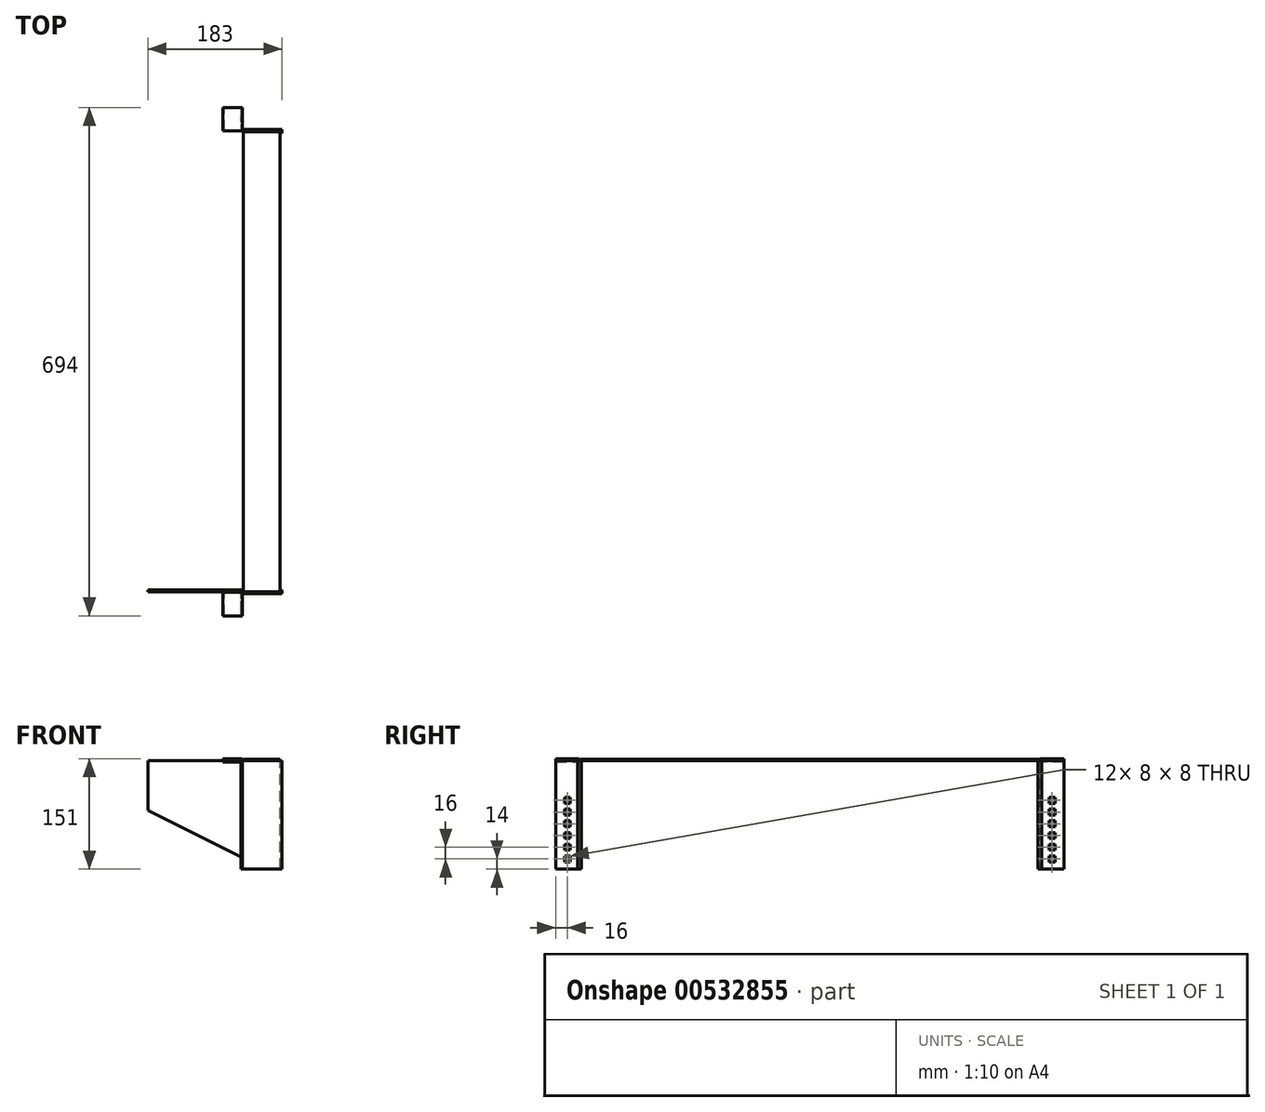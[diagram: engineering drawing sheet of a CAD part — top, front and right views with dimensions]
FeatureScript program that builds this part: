
annotation { "Feature Type Name" : "Feature", "Feature Type Description" : "" }
export const myFeature = defineFeature(function(context is Context, id is Id, definition is map)
    precondition{}
    {
        {
            var Q0;
            Q0=qCreatedBy(makeId("Right.planeOp"),FACE);
            var sketch = newSketch(context, id + "F0", { "sketchPlane" : qUnion([Q0])});
            skLineSegment(sketch, "E0.bottom", {"start": v(-314, 150) * mm, "end": v(314, 150) * mm});
            skLineSegment(sketch, "E0.top", {"start": v(-314, 148) * mm, "end": v(314, 148) * mm});
            skLineSegment(sketch, "E0.left", {"start": v(-314, 150) * mm, "end": v(-314, 148) * mm});
            skLineSegment(sketch, "E0.right", {"start": v(314, 150) * mm, "end": v(314, 148) * mm});
            skLineSegment(sketch, "E1.bottom", {"start": v(-314, 148) * mm, "end": v(-312, 148) * mm});
            skLineSegment(sketch, "E1.top", {"start": v(-314, 0) * mm, "end": v(-312, 0) * mm});
            skLineSegment(sketch, "E1.left", {"start": v(-314, 148) * mm, "end": v(-314, 0) * mm});
            skLineSegment(sketch, "E1.right", {"start": v(-312, 148) * mm, "end": v(-312, 0) * mm});
            skLineSegment(sketch, "E2.bottom", {"start": v(314, 148) * mm, "end": v(312, 148) * mm});
            skLineSegment(sketch, "E2.top", {"start": v(314, 0) * mm, "end": v(312, 0) * mm});
            skLineSegment(sketch, "E2.left", {"start": v(314, 148) * mm, "end": v(314, 0) * mm});
            skLineSegment(sketch, "E2.right", {"start": v(312, 148) * mm, "end": v(312, 0) * mm});
            skSolve(sketch);
        }
        {
            var Q0;
            Q0=makeQuery(id+"F0.imprint","IMPRINT",FACE,{"disambiguationData":[TD([[makeQuery(id+"F0.imprint","IMPRINT",EDGE,{"derivedFrom":sQuery(id+"F0.wireOp",EDGE,"E0.bottom")}),-1.0]])]});
            var Q1;
            Q1=makeQuery(id+"F0.imprint","IMPRINT",FACE,{"disambiguationData":[TD([[makeQuery(id+"F0.imprint","IMPRINT",EDGE,{"derivedFrom":sQuery(id+"F0.wireOp",EDGE,"E2.bottom")}),1.0]])]});
            var Q2;
            Q2=makeQuery(id+"F0.imprint","IMPRINT",FACE,{"disambiguationData":[TD([[makeQuery(id+"F0.imprint","IMPRINT",EDGE,{"derivedFrom":sQuery(id+"F0.wireOp",EDGE,"E1.bottom")}),-1.0]])]});
            extrude(context, id + "F1", {"entities" : qUnion([Q0, Q1, Q2]), "oppositeDirection" : true, "depth" : 50 * mm});
        }
        {
            var Q0;
            Q0=makeQuery(id+"F1.opExtrude","CAP_FACE",FACE,{"disambiguationData":[OSD([sQuery(id+"F0.wireOp",EDGE,"E0.bottom"),sQuery(id+"F0.wireOp",EDGE,"E0.top"),sQuery(id+"F0.wireOp",EDGE,"E0.left"),sQuery(id+"F0.wireOp",EDGE,"E0.right"),sQuery(id+"F0.wireOp",EDGE,"E1.top"),sQuery(id+"F0.wireOp",EDGE,"E1.left"),sQuery(id+"F0.wireOp",EDGE,"E1.right"),sQuery(id+"F0.wireOp",EDGE,"E2.top"),sQuery(id+"F0.wireOp",EDGE,"E2.left"),sQuery(id+"F0.wireOp",EDGE,"E2.right")])],"isStart":false});
            var sketch = newSketch(context, id + "F2", { "sketchPlane" : qUnion([Q0])});
            skLineSegment(sketch, "E3.bottom", {"start": v(314, 0) * mm, "end": v(312, 0) * mm});
            skLineSegment(sketch, "E3.top", {"start": v(314, 150) * mm, "end": v(312, 150) * mm});
            skLineSegment(sketch, "E3.left", {"start": v(314, 0) * mm, "end": v(314, 150) * mm});
            skLineSegment(sketch, "E3.right", {"start": v(312, 0) * mm, "end": v(312, 150) * mm});
            skLineSegment(sketch, "E4.bottom", {"start": v(-312, 0) * mm, "end": v(-314, 0) * mm});
            skLineSegment(sketch, "E4.top", {"start": v(-312, 150) * mm, "end": v(-314, 150) * mm});
            skLineSegment(sketch, "E4.left", {"start": v(-312, 0) * mm, "end": v(-312, 150) * mm});
            skLineSegment(sketch, "E4.right", {"start": v(-314, 0) * mm, "end": v(-314, 150) * mm});
            skSolve(sketch);
        }
        {
            var Q0;
            {var subQ2=sQuery(id+"F2.wireOp",EDGE,"E3.bottom");Q0=makeQuery(id+"F2.imprint","IMPRINT",FACE,{"disambiguationData":[TD([[makeQuery(id+"F2.imprint","IMPRINT",EDGE,{"derivedFrom":subQ2}),-1.0]])]});}
            var Q1;
            {var subQ3=sQuery(id+"F2.wireOp",EDGE,"E4.bottom");Q1=makeQuery(id+"F2.imprint","IMPRINT",FACE,{"disambiguationData":[TD([[makeQuery(id+"F2.imprint","IMPRINT",EDGE,{"derivedFrom":subQ3}),1.0]])]});}
            extrude(context, id + "F3", {"entities" : qUnion([Q0, Q1]), "operationType" : NewBodyOperationType.ADD, "depth" : 130 * mm});
        }
        {
            var Q0;
            Q0=makeQuery(id+"F1.opExtrude","CAP_FACE",FACE,{"disambiguationData":[OSD([sQuery(id+"F0.wireOp",EDGE,"E0.bottom"),sQuery(id+"F0.wireOp",EDGE,"E0.top"),sQuery(id+"F0.wireOp",EDGE,"E0.left"),sQuery(id+"F0.wireOp",EDGE,"E0.right"),sQuery(id+"F0.wireOp",EDGE,"E1.top"),sQuery(id+"F0.wireOp",EDGE,"E1.left"),sQuery(id+"F0.wireOp",EDGE,"E1.right"),sQuery(id+"F0.wireOp",EDGE,"E2.top"),sQuery(id+"F0.wireOp",EDGE,"E2.left"),sQuery(id+"F0.wireOp",EDGE,"E2.right")])],"isStart":true});
            var sketch = newSketch(context, id + "F4", { "sketchPlane" : qUnion([Q0])});
            skLineSegment(sketch, "E5.bottom", {"start": v(314, 0) * mm, "end": v(312, 0) * mm});
            skLineSegment(sketch, "E5.top", {"start": v(314, 148) * mm, "end": v(312, 148) * mm});
            skLineSegment(sketch, "E5.left", {"start": v(314, 0) * mm, "end": v(314, 148) * mm});
            skLineSegment(sketch, "E5.right", {"start": v(312, 0) * mm, "end": v(312, 148) * mm});
            skLineSegment(sketch, "E6.bottom", {"start": v(-312, 0) * mm, "end": v(-314, 0) * mm});
            skLineSegment(sketch, "E6.top", {"start": v(-312, 148) * mm, "end": v(-314, 148) * mm});
            skLineSegment(sketch, "E6.left", {"start": v(-312, 0) * mm, "end": v(-312, 148) * mm});
            skLineSegment(sketch, "E6.right", {"start": v(-314, 0) * mm, "end": v(-314, 148) * mm});
            skSolve(sketch);
        }
        {
            var Q0;
            Q0=makeQuery(id+"F4.imprint","IMPRINT",FACE,{"disambiguationData":[TD([[makeQuery(id+"F4.imprint","IMPRINT",EDGE,{"derivedFrom":sQuery(id+"F4.wireOp",EDGE,"E5.bottom")}),-1.0]])]});
            var Q1;
            Q1=makeQuery(id+"F4.imprint","IMPRINT",FACE,{"disambiguationData":[TD([[makeQuery(id+"F4.imprint","IMPRINT",EDGE,{"derivedFrom":sQuery(id+"F4.wireOp",EDGE,"E6.bottom")}),1.0]])]});
            extrude(context, id + "F5", {"entities" : qUnion([Q0, Q1]), "operationType" : NewBodyOperationType.ADD, "depth" : 3 * mm});
        }
        {
            var Q0;
            Q0=makeQuery(id+"F5.boolean.opBoolean","MERGE",FACE,{"derivedFrom":[makeQuery(id+"F3.boolean.opBoolean","MERGE",FACE,{"derivedFrom":[makeQuery(id+"F1.opExtrude","SWEPT_FACE",FACE,{"disambiguationData":[OSD([sQuery(id+"F0.wireOp",EDGE,"E1.right")])]}),makeQuery(id+"F3.opExtrude","SWEPT_FACE",FACE,{"disambiguationData":[OSD([sQuery(id+"F2.wireOp",EDGE,"E3.right")])]})]}),makeQuery(id+"F5.opExtrude","SWEPT_FACE",FACE,{"disambiguationData":[OSD([sQuery(id+"F4.wireOp",EDGE,"E6.left")])]})]});
            var sketch = newSketch(context, id + "F6", { "sketchPlane" : qUnion([Q0])});
            skLineSegment(sketch, "E7.bottom", {"start": v(-3, 148) * mm, "end": v(-1, 148) * mm});
            skLineSegment(sketch, "E7.top", {"start": v(-3, 0) * mm, "end": v(-1, 0) * mm});
            skLineSegment(sketch, "E7.left", {"start": v(-3, 148) * mm, "end": v(-3, 0) * mm});
            skLineSegment(sketch, "E7.right", {"start": v(-1, 148) * mm, "end": v(-1, 0) * mm});
            skSolve(sketch);
        }
        {
            var Q0;
            Q0=makeQuery(id+"F6.imprint","IMPRINT",FACE,{"disambiguationData":[TD([[makeQuery(id+"F6.imprint","IMPRINT",EDGE,{"derivedFrom":sQuery(id+"F6.wireOp",EDGE,"E7.bottom")}),-1.0]])]});
            extrude(context, id + "F7", {"entities" : qUnion([Q0]), "operationType" : NewBodyOperationType.ADD, "oppositeDirection" : true, "depth" : 5 * mm});
        }
        {
            var Q0;
            Q0=makeQuery(id+"F7.opExtrude","SWEPT_FACE",FACE,{"disambiguationData":[OSD([sQuery(id+"F6.wireOp",EDGE,"E7.right")])]});
            var sketch = newSketch(context, id + "F8", { "sketchPlane" : qUnion([Q0])});
            skLineSegment(sketch, "E8.bottom", {"start": v(315, 0) * mm, "end": v(317, 0) * mm});
            skLineSegment(sketch, "E8.top", {"start": v(315, 148) * mm, "end": v(317, 148) * mm});
            skLineSegment(sketch, "E8.left", {"start": v(317, 0) * mm, "end": v(317, 148) * mm});
            skLineSegment(sketch, "E8.right", {"start": v(315, 0) * mm, "end": v(315, 148) * mm});
            skSolve(sketch);
        }
        {
            var Q0;
            Q0=makeQuery(id+"F8.imprint","IMPRINT",FACE,{"disambiguationData":[TD([[makeQuery(id+"F8.imprint","IMPRINT",EDGE,{"derivedFrom":sQuery(id+"F8.wireOp",EDGE,"E8.bottom")}),-1.0]])]});
            extrude(context, id + "F9", {"entities" : qUnion([Q0]), "operationType" : NewBodyOperationType.ADD, "depth" : 54 * mm});
        }
        {
            var Q0;
            Q0=makeQuery(id+"F9.boolean.opBoolean","MERGE",FACE,{"derivedFrom":[makeQuery(id+"F7.opExtrude","CAP_FACE",FACE,{"disambiguationData":[OSD([sQuery(id+"F6.wireOp",EDGE,"E7.bottom"),sQuery(id+"F6.wireOp",EDGE,"E7.top"),sQuery(id+"F6.wireOp",EDGE,"E7.left"),sQuery(id+"F6.wireOp",EDGE,"E7.right")])],"isStart":false}),makeQuery(id+"F9.opExtrude","SWEPT_FACE",FACE,{"disambiguationData":[OSD([sQuery(id+"F8.wireOp",EDGE,"E8.left")])]})]});
            var sketch = newSketch(context, id + "F10", { "sketchPlane" : qUnion([Q0])});
            skLineSegment(sketch, "E9.bottom", {"start": v(-53, 148) * mm, "end": v(-51, 148) * mm});
            skLineSegment(sketch, "E9.top", {"start": v(-53, 0) * mm, "end": v(-51, 0) * mm});
            skLineSegment(sketch, "E9.left", {"start": v(-53, 148) * mm, "end": v(-53, 0) * mm});
            skLineSegment(sketch, "E9.right", {"start": v(-51, 148) * mm, "end": v(-51, 0) * mm});
            skSolve(sketch);
        }
        {
            var Q0;
            Q0=makeQuery(id+"F10.imprint","IMPRINT",FACE,{"disambiguationData":[TD([[makeQuery(id+"F10.imprint","IMPRINT",EDGE,{"derivedFrom":sQuery(id+"F10.wireOp",EDGE,"E9.bottom")}),1.0]])]});
            extrude(context, id + "F11", {"entities" : qUnion([Q0]), "operationType" : NewBodyOperationType.ADD, "depth" : 30 * mm});
        }
        {
            var Q0;
            Q0=makeQuery(id+"F5.boolean.opBoolean","MERGE",FACE,{"derivedFrom":[makeQuery(id+"F3.boolean.opBoolean","MERGE",FACE,{"derivedFrom":[makeQuery(id+"F1.opExtrude","SWEPT_FACE",FACE,{"disambiguationData":[OSD([sQuery(id+"F0.wireOp",EDGE,"E0.left"),sQuery(id+"F0.wireOp",EDGE,"E1.left")])]}),makeQuery(id+"F3.opExtrude","SWEPT_FACE",FACE,{"disambiguationData":[OSD([sQuery(id+"F2.wireOp",EDGE,"E3.left")])]})]}),makeQuery(id+"F5.opExtrude","SWEPT_FACE",FACE,{"disambiguationData":[OSD([sQuery(id+"F4.wireOp",EDGE,"E6.right")])]})]});
            var sketch = newSketch(context, id + "F12", { "sketchPlane" : qUnion([Q0])});
            skLineSegment(sketch, "E10", {"start": v(0, 0) * mm, "end": v(-20, 0) * mm});
            skLineSegment(sketch, "E11", {"start": v(-20, 0) * mm, "end": v(-180, 80) * mm});
            skLineSegment(sketch, "E12", {"start": v(-180, 80) * mm, "end": v(-180, 0) * mm});
            skLineSegment(sketch, "E13", {"start": v(-180, 0) * mm, "end": v(-20, 0) * mm});
            skSolve(sketch);
        }
        {
            var Q0;
            Q0=makeQuery(id+"F12.imprint","IMPRINT",FACE,{"disambiguationData":[TD([[makeQuery(id+"F12.imprint","IMPRINT",EDGE,{"derivedFrom":sQuery(id+"F12.wireOp",EDGE,"E11")}),1.0]])]});
            extrude(context, id + "F13", {"entities" : qUnion([Q0]), "operationType" : NewBodyOperationType.REMOVE, "oppositeDirection" : true, "depth" : 761 * mm});
        }
        {
            var Q0;
            Q0=makeQuery(id+"F5.boolean.opBoolean","MERGE",FACE,{"derivedFrom":[makeQuery(id+"F3.boolean.opBoolean","MERGE",FACE,{"derivedFrom":[makeQuery(id+"F1.opExtrude","SWEPT_FACE",FACE,{"disambiguationData":[OSD([sQuery(id+"F0.wireOp",EDGE,"E0.right"),sQuery(id+"F0.wireOp",EDGE,"E2.left")])]}),makeQuery(id+"F3.opExtrude","SWEPT_FACE",FACE,{"disambiguationData":[OSD([sQuery(id+"F2.wireOp",EDGE,"E4.right")])]})]}),makeQuery(id+"F5.opExtrude","SWEPT_FACE",FACE,{"disambiguationData":[OSD([sQuery(id+"F4.wireOp",EDGE,"E5.left")])]})]});
            var sketch = newSketch(context, id + "F14", { "sketchPlane" : qUnion([Q0])});
            skLineSegment(sketch, "E14.bottom", {"start": v(-3, 148) * mm, "end": v(-1, 148) * mm});
            skLineSegment(sketch, "E14.top", {"start": v(-3, 0) * mm, "end": v(-1, 0) * mm});
            skLineSegment(sketch, "E14.left", {"start": v(-3, 148) * mm, "end": v(-3, 0) * mm});
            skLineSegment(sketch, "E14.right", {"start": v(-1, 148) * mm, "end": v(-1, 0) * mm});
            skSolve(sketch);
        }
        {
            var Q0;
            Q0=makeQuery(id+"F14.imprint","IMPRINT",FACE,{"disambiguationData":[TD([[makeQuery(id+"F14.imprint","IMPRINT",EDGE,{"derivedFrom":sQuery(id+"F14.wireOp",EDGE,"E14.bottom")}),-1.0]])]});
            extrude(context, id + "F15", {"entities" : qUnion([Q0]), "operationType" : NewBodyOperationType.ADD, "depth" : 3 * mm});
        }
        {
            var Q0;
            Q0=makeQuery(id+"F15.opExtrude","SWEPT_FACE",FACE,{"disambiguationData":[OSD([sQuery(id+"F14.wireOp",EDGE,"E14.right")])]});
            var sketch = newSketch(context, id + "F16", { "sketchPlane" : qUnion([Q0])});
            skLineSegment(sketch, "E15.bottom", {"start": v(-317, 148) * mm, "end": v(-315, 148) * mm});
            skLineSegment(sketch, "E15.top", {"start": v(-317, 0) * mm, "end": v(-315, 0) * mm});
            skLineSegment(sketch, "E15.left", {"start": v(-317, 148) * mm, "end": v(-317, 0) * mm});
            skLineSegment(sketch, "E15.right", {"start": v(-315, 148) * mm, "end": v(-315, 0) * mm});
            skSolve(sketch);
        }
        {
            var Q0;
            Q0=qSketchRegion(id+"F16",true);
            extrude(context, id + "F17", {"entities" : qUnion([Q0]), "operationType" : NewBodyOperationType.ADD, "depth" : 54 * mm});
        }
        {
            var Q0;
            Q0=makeQuery(id+"F17.boolean.opBoolean","MERGE",FACE,{"derivedFrom":[makeQuery(id+"F15.opExtrude","CAP_FACE",FACE,{"disambiguationData":[OSD([sQuery(id+"F14.wireOp",EDGE,"E14.bottom"),sQuery(id+"F14.wireOp",EDGE,"E14.top"),sQuery(id+"F14.wireOp",EDGE,"E14.left"),sQuery(id+"F14.wireOp",EDGE,"E14.right")])],"isStart":false}),makeQuery(id+"F17.opExtrude","SWEPT_FACE",FACE,{"disambiguationData":[OSD([sQuery(id+"F16.wireOp",EDGE,"E15.left")])]})]});
            var sketch = newSketch(context, id + "F18", { "sketchPlane" : qUnion([Q0])});
            skLineSegment(sketch, "E16.bottom", {"start": v(53, 148) * mm, "end": v(51, 148) * mm});
            skLineSegment(sketch, "E16.top", {"start": v(53, 0) * mm, "end": v(51, 0) * mm});
            skLineSegment(sketch, "E16.left", {"start": v(53, 148) * mm, "end": v(53, 0) * mm});
            skLineSegment(sketch, "E16.right", {"start": v(51, 148) * mm, "end": v(51, 0) * mm});
            skSolve(sketch);
        }
        {
            var Q0;
            Q0=makeQuery(id+"F18.imprint","IMPRINT",FACE,{"disambiguationData":[TD([[makeQuery(id+"F18.imprint","IMPRINT",EDGE,{"derivedFrom":sQuery(id+"F18.wireOp",EDGE,"E16.bottom")}),-1.0]])]});
            extrude(context, id + "F19", {"entities" : qUnion([Q0]), "operationType" : NewBodyOperationType.ADD, "depth" : 30 * mm});
        }
        {
            var Q0;
            Q0=makeQuery(id+"F19.boolean.opBoolean","MERGE",FACE,{"derivedFrom":[makeQuery(id+"F17.opExtrude","CAP_FACE",FACE,{"disambiguationData":[OSD([sQuery(id+"F16.wireOp",EDGE,"E15.bottom"),sQuery(id+"F16.wireOp",EDGE,"E15.top"),sQuery(id+"F16.wireOp",EDGE,"E15.left"),sQuery(id+"F16.wireOp",EDGE,"E15.right")])],"isStart":false}),makeQuery(id+"F19.opExtrude","SWEPT_FACE",FACE,{"disambiguationData":[OSD([sQuery(id+"F18.wireOp",EDGE,"E16.left")])]})]});
            var sketch = newSketch(context, id + "F20", { "sketchPlane" : qUnion([Q0])});
            skLineSegment(sketch, "E17.bottom", {"start": v(-347, 148) * mm, "end": v(-315, 148) * mm});
            skLineSegment(sketch, "E17.top", {"start": v(-347, 146) * mm, "end": v(-315, 146) * mm});
            skLineSegment(sketch, "E17.left", {"start": v(-347, 148) * mm, "end": v(-347, 146) * mm});
            skLineSegment(sketch, "E17.right", {"start": v(-315, 148) * mm, "end": v(-315, 146) * mm});
            skSolve(sketch);
        }
        {
            var Q0;
            Q0=makeQuery(id+"F20.imprint","IMPRINT",FACE,{"disambiguationData":[TD([[makeQuery(id+"F20.imprint","IMPRINT",EDGE,{"derivedFrom":sQuery(id+"F20.wireOp",EDGE,"E17.bottom")}),-1.0]])]});
            extrude(context, id + "F21", {"entities" : qUnion([Q0]), "operationType" : NewBodyOperationType.ADD, "depth" : 25 * mm});
        }
        {
            var Q0;
            Q0=makeQuery(id+"F21.boolean.opBoolean","MERGE",FACE,{"derivedFrom":[makeQuery(id+"F19.boolean.opBoolean","MERGE",FACE,{"derivedFrom":[makeQuery(id+"F17.boolean.opBoolean","MERGE",FACE,{"derivedFrom":[makeQuery(id+"F15.boolean.opBoolean","MERGE",FACE,{"derivedFrom":[makeQuery(id+"F5.opExtrude","SWEPT_FACE",FACE,{"disambiguationData":[OSD([sQuery(id+"F4.wireOp",EDGE,"E5.top")])]}),makeQuery(id+"F15.opExtrude","SWEPT_FACE",FACE,{"disambiguationData":[OSD([sQuery(id+"F14.wireOp",EDGE,"E14.bottom")])]})]}),makeQuery(id+"F17.opExtrude","SWEPT_FACE",FACE,{"disambiguationData":[OSD([sQuery(id+"F16.wireOp",EDGE,"E15.bottom")])]})]}),makeQuery(id+"F19.opExtrude","SWEPT_FACE",FACE,{"disambiguationData":[OSD([sQuery(id+"F18.wireOp",EDGE,"E16.bottom")])]})]}),makeQuery(id+"F21.opExtrude","SWEPT_FACE",FACE,{"disambiguationData":[OSD([sQuery(id+"F20.wireOp",EDGE,"E17.bottom")])]})]});
            var sketch = newSketch(context, id + "F22", { "sketchPlane" : qUnion([Q0])});
            skLineSegment(sketch, "E18.bottom", {"start": v(-78, 315) * mm, "end": v(-76, 315) * mm});
            skLineSegment(sketch, "E18.top", {"start": v(-78, 347) * mm, "end": v(-76, 347) * mm});
            skLineSegment(sketch, "E18.left", {"start": v(-78, 315) * mm, "end": v(-78, 347) * mm});
            skLineSegment(sketch, "E18.right", {"start": v(-76, 315) * mm, "end": v(-76, 347) * mm});
            skSolve(sketch);
        }
        {
            var Q0;
            Q0=makeQuery(id+"F22.imprint","IMPRINT",FACE,{"disambiguationData":[TD([[makeQuery(id+"F22.imprint","IMPRINT",EDGE,{"derivedFrom":sQuery(id+"F22.wireOp",EDGE,"E18.bottom")}),1.0]])]});
            extrude(context, id + "F23", {"entities" : qUnion([Q0]), "operationType" : NewBodyOperationType.ADD, "depth" : 3 * mm});
        }
        {
            var Q0;
            Q0=makeQuery(id+"F23.opExtrude","SWEPT_FACE",FACE,{"disambiguationData":[OSD([sQuery(id+"F22.wireOp",EDGE,"E18.right")])]});
            var sketch = newSketch(context, id + "F24", { "sketchPlane" : qUnion([Q0])});
            skLineSegment(sketch, "E19.bottom", {"start": v(347, 151) * mm, "end": v(315, 151) * mm});
            skLineSegment(sketch, "E19.top", {"start": v(347, 149) * mm, "end": v(315, 149) * mm});
            skLineSegment(sketch, "E19.left", {"start": v(347, 151) * mm, "end": v(347, 149) * mm});
            skLineSegment(sketch, "E19.right", {"start": v(315, 151) * mm, "end": v(315, 149) * mm});
            skSolve(sketch);
        }
        {
            var Q0;
            Q0=makeQuery(id+"F24.imprint","IMPRINT",FACE,{"disambiguationData":[TD([[makeQuery(id+"F24.imprint","IMPRINT",EDGE,{"derivedFrom":sQuery(id+"F24.wireOp",EDGE,"E19.bottom")}),-1.0]])]});
            extrude(context, id + "F25", {"entities" : qUnion([Q0]), "operationType" : NewBodyOperationType.ADD, "depth" : 25 * mm});
        }
        {
            var Q0;
            Q0=makeQuery(id+"F19.boolean.opBoolean","MERGE",FACE,{"derivedFrom":[makeQuery(id+"F17.opExtrude","CAP_FACE",FACE,{"disambiguationData":[OSD([sQuery(id+"F16.wireOp",EDGE,"E15.bottom"),sQuery(id+"F16.wireOp",EDGE,"E15.top"),sQuery(id+"F16.wireOp",EDGE,"E15.left"),sQuery(id+"F16.wireOp",EDGE,"E15.right")])],"isStart":false}),makeQuery(id+"F19.opExtrude","SWEPT_FACE",FACE,{"disambiguationData":[OSD([sQuery(id+"F18.wireOp",EDGE,"E16.left")])]})]});
            var sketch = newSketch(context, id + "F26", { "sketchPlane" : qUnion([Q0])});
            skLineSegment(sketch, "E20.bottom", {"start": v(-327, 10) * mm, "end": v(-335, 10) * mm});
            skLineSegment(sketch, "E20.top", {"start": v(-327, 18) * mm, "end": v(-335, 18) * mm});
            skLineSegment(sketch, "E20.left", {"start": v(-327, 10) * mm, "end": v(-327, 18) * mm});
            skLineSegment(sketch, "E20.right", {"start": v(-335, 10) * mm, "end": v(-335, 18) * mm});
            skLineSegment(sketch, "E21.bottom", {"start": v(-327, 26) * mm, "end": v(-335, 26) * mm});
            skLineSegment(sketch, "E21.top", {"start": v(-327, 34) * mm, "end": v(-335, 34) * mm});
            skLineSegment(sketch, "E21.left", {"start": v(-327, 26) * mm, "end": v(-327, 34) * mm});
            skLineSegment(sketch, "E21.right", {"start": v(-335, 26) * mm, "end": v(-335, 34) * mm});
            skLineSegment(sketch, "E22.bottom", {"start": v(-327, 42) * mm, "end": v(-335, 42) * mm});
            skLineSegment(sketch, "E22.top", {"start": v(-327, 50) * mm, "end": v(-335, 50) * mm});
            skLineSegment(sketch, "E22.left", {"start": v(-327, 42) * mm, "end": v(-327, 50) * mm});
            skLineSegment(sketch, "E22.right", {"start": v(-335, 42) * mm, "end": v(-335, 50) * mm});
            skLineSegment(sketch, "E23.bottom", {"start": v(-327, 58) * mm, "end": v(-335, 58) * mm});
            skLineSegment(sketch, "E23.top", {"start": v(-327, 66) * mm, "end": v(-335, 66) * mm});
            skLineSegment(sketch, "E23.left", {"start": v(-327, 58) * mm, "end": v(-327, 66) * mm});
            skLineSegment(sketch, "E23.right", {"start": v(-335, 58) * mm, "end": v(-335, 66) * mm});
            skLineSegment(sketch, "E24.bottom", {"start": v(-335, 74) * mm, "end": v(-327, 74) * mm});
            skLineSegment(sketch, "E24.top", {"start": v(-335, 82) * mm, "end": v(-327, 82) * mm});
            skLineSegment(sketch, "E24.left", {"start": v(-335, 74) * mm, "end": v(-335, 82) * mm});
            skLineSegment(sketch, "E24.right", {"start": v(-327, 74) * mm, "end": v(-327, 82) * mm});
            skLineSegment(sketch, "E25.bottom", {"start": v(-327, 90) * mm, "end": v(-335, 90) * mm});
            skLineSegment(sketch, "E25.top", {"start": v(-327, 98) * mm, "end": v(-335, 98) * mm});
            skLineSegment(sketch, "E25.left", {"start": v(-327, 90) * mm, "end": v(-327, 98) * mm});
            skLineSegment(sketch, "E25.right", {"start": v(-335, 90) * mm, "end": v(-335, 98) * mm});
            skSolve(sketch);
        }
        {
            var Q0;
            Q0=makeQuery(id+"F26.imprint","IMPRINT",FACE,{"disambiguationData":[TD([[makeQuery(id+"F26.imprint","IMPRINT",EDGE,{"derivedFrom":sQuery(id+"F26.wireOp",EDGE,"E25.bottom")}),-1.0]])]});
            var Q1;
            Q1=makeQuery(id+"F26.imprint","IMPRINT",FACE,{"disambiguationData":[TD([[makeQuery(id+"F26.imprint","IMPRINT",EDGE,{"derivedFrom":sQuery(id+"F26.wireOp",EDGE,"E24.bottom")}),1.0]])]});
            var Q2;
            Q2=makeQuery(id+"F26.imprint","IMPRINT",FACE,{"disambiguationData":[TD([[makeQuery(id+"F26.imprint","IMPRINT",EDGE,{"derivedFrom":sQuery(id+"F26.wireOp",EDGE,"E23.bottom")}),-1.0]])]});
            var Q3;
            Q3=makeQuery(id+"F26.imprint","IMPRINT",FACE,{"disambiguationData":[TD([[makeQuery(id+"F26.imprint","IMPRINT",EDGE,{"derivedFrom":sQuery(id+"F26.wireOp",EDGE,"E22.bottom")}),-1.0]])]});
            var Q4;
            Q4=makeQuery(id+"F26.imprint","IMPRINT",FACE,{"disambiguationData":[TD([[makeQuery(id+"F26.imprint","IMPRINT",EDGE,{"derivedFrom":sQuery(id+"F26.wireOp",EDGE,"E21.bottom")}),-1.0]])]});
            var Q5;
            Q5=makeQuery(id+"F26.imprint","IMPRINT",FACE,{"disambiguationData":[TD([[makeQuery(id+"F26.imprint","IMPRINT",EDGE,{"derivedFrom":sQuery(id+"F26.wireOp",EDGE,"E20.bottom")}),-1.0]])]});
            extrude(context, id + "F27", {"entities" : qUnion([Q0, Q1, Q2, Q3, Q4, Q5]), "operationType" : NewBodyOperationType.REMOVE, "oppositeDirection" : true, "depth" : 25 * mm});
        }
        {
            var Q0;
            Q0=makeQuery(id+"F11.boolean.opBoolean","MERGE",FACE,{"derivedFrom":[makeQuery(id+"F9.opExtrude","CAP_FACE",FACE,{"disambiguationData":[OSD([sQuery(id+"F8.wireOp",EDGE,"E8.bottom"),sQuery(id+"F8.wireOp",EDGE,"E8.top"),sQuery(id+"F8.wireOp",EDGE,"E8.left"),sQuery(id+"F8.wireOp",EDGE,"E8.right")])],"isStart":false}),makeQuery(id+"F11.opExtrude","SWEPT_FACE",FACE,{"disambiguationData":[OSD([sQuery(id+"F10.wireOp",EDGE,"E9.left")])]})]});
            var sketch = newSketch(context, id + "F28", { "sketchPlane" : qUnion([Q0])});
            skLineSegment(sketch, "E26.bottom", {"start": v(347, 148) * mm, "end": v(315, 148) * mm});
            skLineSegment(sketch, "E26.top", {"start": v(347, 146) * mm, "end": v(315, 146) * mm});
            skLineSegment(sketch, "E26.left", {"start": v(347, 148) * mm, "end": v(347, 146) * mm});
            skLineSegment(sketch, "E26.right", {"start": v(315, 148) * mm, "end": v(315, 146) * mm});
            skSolve(sketch);
        }
        {
            var Q0;
            Q0=qSketchRegion(id+"F28",true);
            extrude(context, id + "F29", {"entities" : qUnion([Q0]), "operationType" : NewBodyOperationType.ADD, "depth" : 25 * mm});
        }
        {
            var Q0;
            Q0=makeQuery(id+"F29.boolean.opBoolean","MERGE",FACE,{"derivedFrom":[makeQuery(id+"F11.boolean.opBoolean","MERGE",FACE,{"derivedFrom":[makeQuery(id+"F9.boolean.opBoolean","MERGE",FACE,{"derivedFrom":[makeQuery(id+"F7.boolean.opBoolean","MERGE",FACE,{"derivedFrom":[makeQuery(id+"F5.opExtrude","SWEPT_FACE",FACE,{"disambiguationData":[OSD([sQuery(id+"F4.wireOp",EDGE,"E6.top")])]}),makeQuery(id+"F7.opExtrude","SWEPT_FACE",FACE,{"disambiguationData":[OSD([sQuery(id+"F6.wireOp",EDGE,"E7.bottom")])]})]}),makeQuery(id+"F9.opExtrude","SWEPT_FACE",FACE,{"disambiguationData":[OSD([sQuery(id+"F8.wireOp",EDGE,"E8.top")])]})]}),makeQuery(id+"F11.opExtrude","SWEPT_FACE",FACE,{"disambiguationData":[OSD([sQuery(id+"F10.wireOp",EDGE,"E9.bottom")])]})]}),makeQuery(id+"F29.opExtrude","SWEPT_FACE",FACE,{"disambiguationData":[OSD([sQuery(id+"F28.wireOp",EDGE,"E26.bottom")])]})]});
            var sketch = newSketch(context, id + "F30", { "sketchPlane" : qUnion([Q0])});
            skLineSegment(sketch, "E27.bottom", {"start": v(-78, -347) * mm, "end": v(-76, -347) * mm});
            skLineSegment(sketch, "E27.top", {"start": v(-78, -315) * mm, "end": v(-76, -315) * mm});
            skLineSegment(sketch, "E27.left", {"start": v(-78, -347) * mm, "end": v(-78, -315) * mm});
            skLineSegment(sketch, "E27.right", {"start": v(-76, -347) * mm, "end": v(-76, -315) * mm});
            skSolve(sketch);
        }
        {
            var Q0;
            Q0=qSketchRegion(id+"F30",true);
            extrude(context, id + "F31", {"entities" : qUnion([Q0]), "operationType" : NewBodyOperationType.ADD, "depth" : 3 * mm});
        }
        {
            var Q0;
            Q0=makeQuery(id+"F31.opExtrude","SWEPT_FACE",FACE,{"disambiguationData":[OSD([sQuery(id+"F30.wireOp",EDGE,"E27.right")])]});
            var sketch = newSketch(context, id + "F32", { "sketchPlane" : qUnion([Q0])});
            skLineSegment(sketch, "E28.bottom", {"start": v(-347, 151) * mm, "end": v(-315, 151) * mm});
            skLineSegment(sketch, "E28.top", {"start": v(-347, 149) * mm, "end": v(-315, 149) * mm});
            skLineSegment(sketch, "E28.left", {"start": v(-347, 151) * mm, "end": v(-347, 149) * mm});
            skLineSegment(sketch, "E28.right", {"start": v(-315, 151) * mm, "end": v(-315, 149) * mm});
            skSolve(sketch);
        }
        {
            var Q0;
            Q0=qSketchRegion(id+"F32",true);
            extrude(context, id + "F33", {"entities" : qUnion([Q0]), "operationType" : NewBodyOperationType.ADD, "depth" : 25 * mm});
        }
        {
            var Q0;
            Q0=makeQuery(id+"F11.boolean.opBoolean","MERGE",FACE,{"derivedFrom":[makeQuery(id+"F9.opExtrude","CAP_FACE",FACE,{"disambiguationData":[OSD([sQuery(id+"F8.wireOp",EDGE,"E8.bottom"),sQuery(id+"F8.wireOp",EDGE,"E8.top"),sQuery(id+"F8.wireOp",EDGE,"E8.left"),sQuery(id+"F8.wireOp",EDGE,"E8.right")])],"isStart":false}),makeQuery(id+"F11.opExtrude","SWEPT_FACE",FACE,{"disambiguationData":[OSD([sQuery(id+"F10.wireOp",EDGE,"E9.left")])]})]});
            var sketch = newSketch(context, id + "F34", { "sketchPlane" : qUnion([Q0])});
            skLineSegment(sketch, "E29.bottom", {"start": v(335, 10) * mm, "end": v(327, 10) * mm});
            skLineSegment(sketch, "E29.top", {"start": v(335, 18) * mm, "end": v(327, 18) * mm});
            skLineSegment(sketch, "E29.left", {"start": v(335, 10) * mm, "end": v(335, 18) * mm});
            skLineSegment(sketch, "E29.right", {"start": v(327, 10) * mm, "end": v(327, 18) * mm});
            skLineSegment(sketch, "E30.1.0.0", {"start": v(335, 26) * mm, "end": v(327, 26) * mm});
            skLineSegment(sketch, "E30.1.0.1", {"start": v(335, 26) * mm, "end": v(335, 34) * mm});
            skLineSegment(sketch, "E30.1.0.2", {"start": v(335, 34) * mm, "end": v(327, 34) * mm});
            skLineSegment(sketch, "E30.1.0.3", {"start": v(327, 26) * mm, "end": v(327, 34) * mm});
            skLineSegment(sketch, "E30.2.0.0", {"start": v(335, 42) * mm, "end": v(327, 42) * mm});
            skLineSegment(sketch, "E30.2.0.1", {"start": v(335, 42) * mm, "end": v(335, 50) * mm});
            skLineSegment(sketch, "E30.2.0.2", {"start": v(335, 50) * mm, "end": v(327, 50) * mm});
            skLineSegment(sketch, "E30.2.0.3", {"start": v(327, 42) * mm, "end": v(327, 50) * mm});
            skLineSegment(sketch, "E30.3.0.0", {"start": v(335, 58) * mm, "end": v(327, 58) * mm});
            skLineSegment(sketch, "E30.3.0.1", {"start": v(335, 58) * mm, "end": v(335, 66) * mm});
            skLineSegment(sketch, "E30.3.0.2", {"start": v(335, 66) * mm, "end": v(327, 66) * mm});
            skLineSegment(sketch, "E30.3.0.3", {"start": v(327, 58) * mm, "end": v(327, 66) * mm});
            skLineSegment(sketch, "E30.4.0.0", {"start": v(335, 74) * mm, "end": v(327, 74) * mm});
            skLineSegment(sketch, "E30.4.0.1", {"start": v(335, 74) * mm, "end": v(335, 82) * mm});
            skLineSegment(sketch, "E30.4.0.2", {"start": v(335, 82) * mm, "end": v(327, 82) * mm});
            skLineSegment(sketch, "E30.4.0.3", {"start": v(327, 74) * mm, "end": v(327, 82) * mm});
            skLineSegment(sketch, "E30.5.0.0", {"start": v(335, 90) * mm, "end": v(327, 90) * mm});
            skLineSegment(sketch, "E30.5.0.1", {"start": v(335, 90) * mm, "end": v(335, 98) * mm});
            skLineSegment(sketch, "E30.5.0.2", {"start": v(335, 98) * mm, "end": v(327, 98) * mm});
            skLineSegment(sketch, "E30.5.0.3", {"start": v(327, 90) * mm, "end": v(327, 98) * mm});
            skLineSegment(sketch, "E30.direction1", {"start": v(327, 10) * mm, "end": v(327, 26) * mm, "construction": true});
            skSolve(sketch);
        }
        {
            var Q0;
            Q0=makeQuery(id+"F34.imprint","IMPRINT",FACE,{"disambiguationData":[TD([[makeQuery(id+"F34.imprint","IMPRINT",EDGE,{"derivedFrom":sQuery(id+"F34.wireOp",EDGE,"E30.4.0.0")}),-1.0]])]});
            var Q1;
            Q1=makeQuery(id+"F34.imprint","IMPRINT",FACE,{"disambiguationData":[TD([[makeQuery(id+"F34.imprint","IMPRINT",EDGE,{"derivedFrom":sQuery(id+"F34.wireOp",EDGE,"E30.3.0.0")}),-1.0]])]});
            var Q2;
            Q2=makeQuery(id+"F34.imprint","IMPRINT",FACE,{"disambiguationData":[TD([[makeQuery(id+"F34.imprint","IMPRINT",EDGE,{"derivedFrom":sQuery(id+"F34.wireOp",EDGE,"E30.2.0.0")}),-1.0]])]});
            var Q3;
            Q3=makeQuery(id+"F34.imprint","IMPRINT",FACE,{"disambiguationData":[TD([[makeQuery(id+"F34.imprint","IMPRINT",EDGE,{"derivedFrom":sQuery(id+"F34.wireOp",EDGE,"E30.1.0.0")}),-1.0]])]});
            var Q4;
            Q4=makeQuery(id+"F34.imprint","IMPRINT",FACE,{"disambiguationData":[TD([[makeQuery(id+"F34.imprint","IMPRINT",EDGE,{"derivedFrom":sQuery(id+"F34.wireOp",EDGE,"E29.bottom")}),-1.0]])]});
            var Q5;
            Q5=makeQuery(id+"F34.imprint","IMPRINT",FACE,{"disambiguationData":[TD([[makeQuery(id+"F34.imprint","IMPRINT",EDGE,{"derivedFrom":sQuery(id+"F34.wireOp",EDGE,"E30.5.0.0")}),-1.0]])]});
            extrude(context, id + "F35", {"entities" : qUnion([Q0, Q1, Q2, Q3, Q4, Q5]), "operationType" : NewBodyOperationType.REMOVE, "oppositeDirection" : true, "depth" : 25 * mm});
        }
        {
            var Q0;
            Q0=makeQuery(id+"F5.boolean.opBoolean","MERGE",FACE,{"derivedFrom":[makeQuery(id+"F3.boolean.opBoolean","MERGE",FACE,{"derivedFrom":[makeQuery(id+"F1.opExtrude","SWEPT_FACE",FACE,{"disambiguationData":[OSD([sQuery(id+"F0.wireOp",EDGE,"E0.left"),sQuery(id+"F0.wireOp",EDGE,"E1.left")])]}),makeQuery(id+"F3.opExtrude","SWEPT_FACE",FACE,{"disambiguationData":[OSD([sQuery(id+"F2.wireOp",EDGE,"E3.left")])]})]}),makeQuery(id+"F5.opExtrude","SWEPT_FACE",FACE,{"disambiguationData":[OSD([sQuery(id+"F4.wireOp",EDGE,"E6.right")])]})]});
            var sketch = newSketch(context, id + "F36", { "sketchPlane" : qUnion([Q0])});
            skPoint(sketch, "E31", {"position": v(-100, 85) * mm});
            skSolve(sketch);
        }
        {
            var Q0;
            Q0=sQuery(id+"F36.wireOp",VERTEX,"E31");
            var Q1;
            Q1=makeQuery(id+"F1.opExtrude","SWEPT_BODY",BODY,{"disambiguationData":[OSD([sQuery(id+"F0.wireOp",EDGE,"E0.bottom"),sQuery(id+"F0.wireOp",EDGE,"E0.top"),sQuery(id+"F0.wireOp",EDGE,"E0.left"),sQuery(id+"F0.wireOp",EDGE,"E0.right"),sQuery(id+"F0.wireOp",EDGE,"E1.top"),sQuery(id+"F0.wireOp",EDGE,"E1.left"),sQuery(id+"F0.wireOp",EDGE,"E1.right"),sQuery(id+"F0.wireOp",EDGE,"E2.top"),sQuery(id+"F0.wireOp",EDGE,"E2.left"),sQuery(id+"F0.wireOp",EDGE,"E2.right")])]});
            hole(context, id + "F37", {"style" : HoleStyle.SIMPLE, "endStyle" : HoleEndStyle.THROUGH, "holeDiameter" : 8 * mm, "isTappedThrough" : true, "tappedDepth" : 12 * mm, "tapClearance" : 3, "locations" : qUnion([Q0]), "scope" : qUnion([Q1])});
        }
    });
